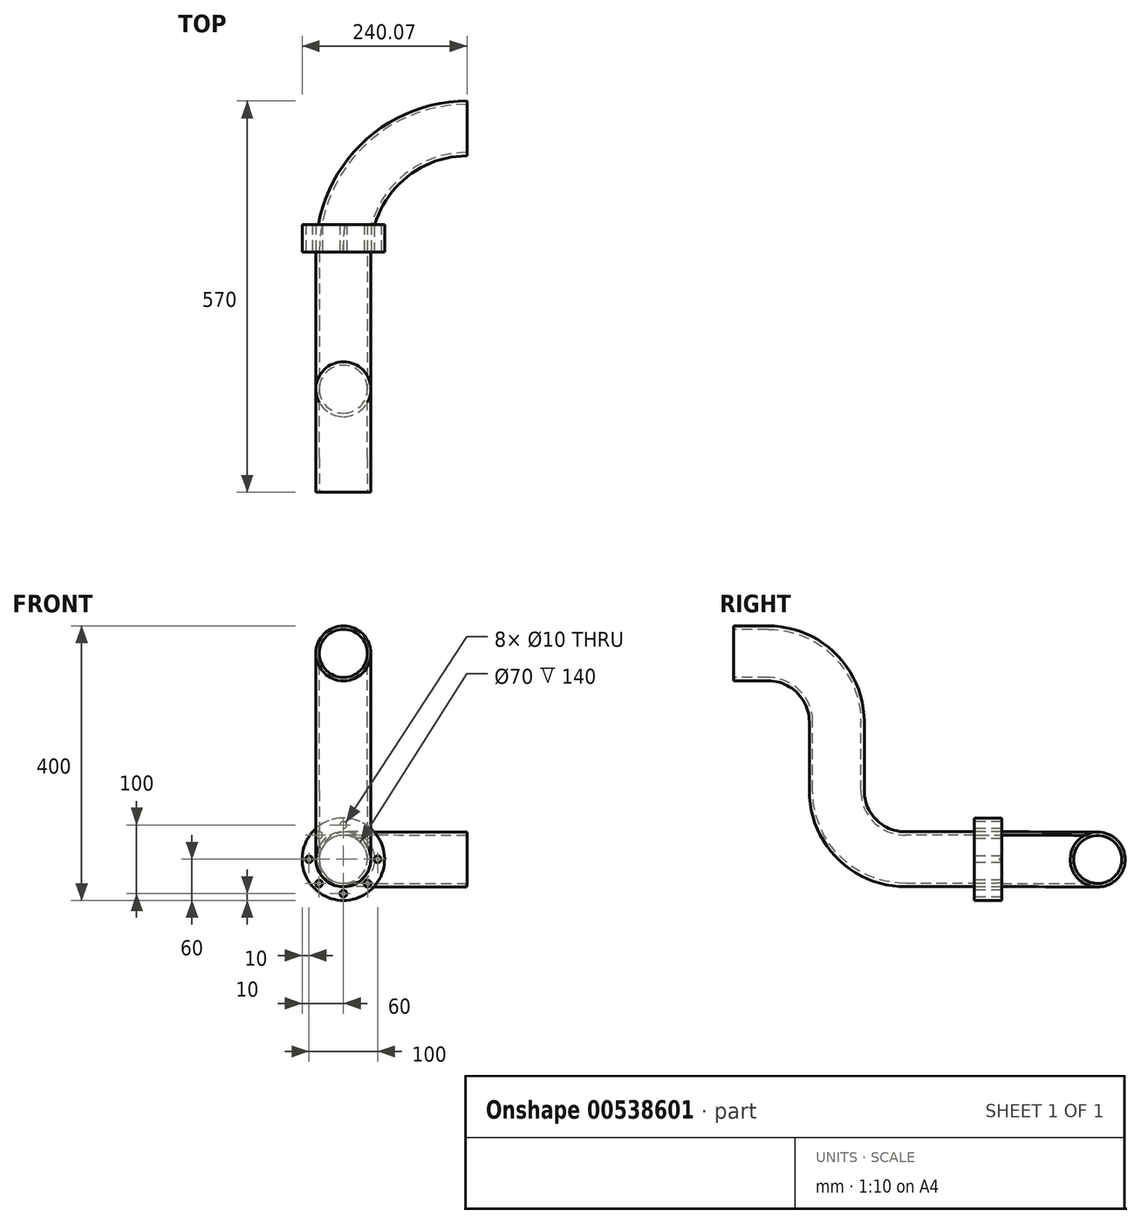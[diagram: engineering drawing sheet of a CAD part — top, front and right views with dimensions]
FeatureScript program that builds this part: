
annotation { "Feature Type Name" : "Feature", "Feature Type Description" : "" }
export const myFeature = defineFeature(function(context is Context, id is Id, definition is map)
    precondition{}
    {
        {
            var Q0;
            Q0=qCreatedBy(makeId("Front.planeOp"),FACE);
            var sketch = newSketch(context, id + "F0", { "sketchPlane" : qUnion([Q0])});
            skCircle(sketch, "E0", {"center": v(0, 0) * mm, "radius": 60 * mm});
            skCircle(sketch, "E1", {"center": v(0, 50) * mm, "radius": 5 * mm});
            skCircle(sketch, "E2.1.0", {"center": v(-35.36, 35.36) * mm, "radius": 5 * mm});
            skCircle(sketch, "E2.2.0", {"center": v(-50, 0) * mm, "radius": 5 * mm});
            skCircle(sketch, "E2.3.0", {"center": v(-35.36, -35.36) * mm, "radius": 5 * mm});
            skCircle(sketch, "E2.4.0", {"center": v(0, -50) * mm, "radius": 5 * mm});
            skCircle(sketch, "E2.5.0", {"center": v(35.36, -35.36) * mm, "radius": 5 * mm});
            skCircle(sketch, "E2.6.0", {"center": v(50, 0) * mm, "radius": 5 * mm});
            skCircle(sketch, "E2.7.0", {"center": v(35.36, 35.36) * mm, "radius": 5 * mm});
            skCircle(sketch, "E3", {"center": v(0, 0) * mm, "radius": 35 * mm});
            skSolve(sketch);
        }
        {
            var Q0;
            Q0 = qSketchRegion(id + "F0", true);
            extrude(context, id + "F1", {"entities" : qUnion([Q0]), "oppositeDirection" : true, "depth" : 20 * mm, "offsetDistance" : 25 * mm});
        }
        {
            var Q0;
            Q0=qCreatedBy(makeId("Front.planeOp"),FACE);
            var sketch = newSketch(context, id + "F2", { "sketchPlane" : qUnion([Q0])});
            skCircle(sketch, "E4", {"center": v(0, 0) * mm, "radius": 35 * mm});
            skCircle(sketch, "E5", {"center": v(0, 0) * mm, "radius": 40 * mm});
            skSolve(sketch);
        }
        {
            var Q0;
            Q0=qCreatedBy(makeId("Right.planeOp"),FACE);
            var sketch = newSketch(context, id + "F3", { "sketchPlane" : qUnion([Q0])});
            skLineSegment(sketch, "E6", {"start": v(0, 0) * mm, "end": v(-100, 0) * mm});
            skLineSegment(sketch, "E7", {"start": v(-200, 100) * mm, "end": v(-200, 200) * mm});
            skLineSegment(sketch, "E8", {"start": v(-300, 300) * mm, "end": v(-350, 300) * mm});
            skPoint(sketch, "E9.visualSharp", {"position": v(-200, 0) * mm});
            skArc(sketch, "E9.filletArc", {"start": v(-200, 100) * mm, "mid": v(-170.71, 29.29) * mm, "end": v(-100, 0) * mm});
            skPoint(sketch, "E10.visualSharp", {"position": v(-200, 300) * mm});
            skArc(sketch, "E10.filletArc", {"start": v(-200, 200) * mm, "mid": v(-229.29, 270.71) * mm, "end": v(-300, 300) * mm});
            skSolve(sketch);
        }
        {
            var Q0;
            Q0=makeQuery(id+"F2.imprint","IMPRINT",FACE,{"disambiguationData":[TD([[makeQuery(id+"F2.imprint","IMPRINT",EDGE,{"derivedFrom":sQuery(id+"F2.wireOp",EDGE,"E4")}),-1.0]])]});
            var Q1;
            Q1=sQuery(id+"F3.wireOp",EDGE,"E9.filletArc");
            var Q2;
            Q2=sQuery(id+"F3.wireOp",EDGE,"E7");
            var Q3;
            Q3=sQuery(id+"F3.wireOp",EDGE,"E10.filletArc");
            var Q4;
            Q4=sQuery(id+"F3.wireOp",EDGE,"E8");
            var Q5;
            Q5=sQuery(id+"F3.wireOp",EDGE,"E6");
            sweep(context, id + "F4", {"operationType" : NewBodyOperationType.ADD, "profiles" : qUnion([Q0]), "path" : qUnion([Q1, Q2, Q3, Q4, Q5])});
        }
        {
            var Q0;
            Q0=makeQuery(id+"F1.opExtrude","CAP_FACE",FACE,{"disambiguationData":[OSD([sQuery(id+"F0.wireOp",EDGE,"E0"),sQuery(id+"F0.wireOp",EDGE,"E1"),sQuery(id+"F0.wireOp",EDGE,"E2.1.0"),sQuery(id+"F0.wireOp",EDGE,"E2.2.0"),sQuery(id+"F0.wireOp",EDGE,"E2.3.0"),sQuery(id+"F0.wireOp",EDGE,"E2.4.0"),sQuery(id+"F0.wireOp",EDGE,"E2.5.0"),sQuery(id+"F0.wireOp",EDGE,"E2.6.0"),sQuery(id+"F0.wireOp",EDGE,"E2.7.0"),sQuery(id+"F0.wireOp",EDGE,"E3")])],"isStart":false});
            extrude(context, id + "F5", {"entities" : qUnion([Q0]), "depth" : 20 * mm, "offsetDistance" : 25 * mm});
        }
        {
            var Q0;
            Q0=qCreatedBy(makeId("Front.planeOp"),FACE);
            var sketch = newSketch(context, id + "F6", { "sketchPlane" : qUnion([Q0])});
            skCircle(sketch, "E11", {"center": v(0, 0) * mm, "radius": 35 * mm});
            skCircle(sketch, "E12", {"center": v(0, 0) * mm, "radius": 40 * mm});
            skLineSegment(sketch, "E13", {"start": v(179.87, -78.02) * mm, "end": v(180.13, 76.73) * mm, "construction": true});
            skSolve(sketch);
        }
        {
            var Q0;
            Q0 = qSketchRegion(id + "F6", true);
            var Q1;
            Q1=sQuery(id+"F6.wireOp",EDGE,"E13");
            revolve(context, id + "F7", {"operationType" : NewBodyOperationType.ADD, "entities" : qUnion([Q0]), "axis" : qUnion([Q1]), "revolveType" : RevolveType.ONE_DIRECTION, "oppositeDirection" : true, "angle" : 90 * degree});
        }
    });
